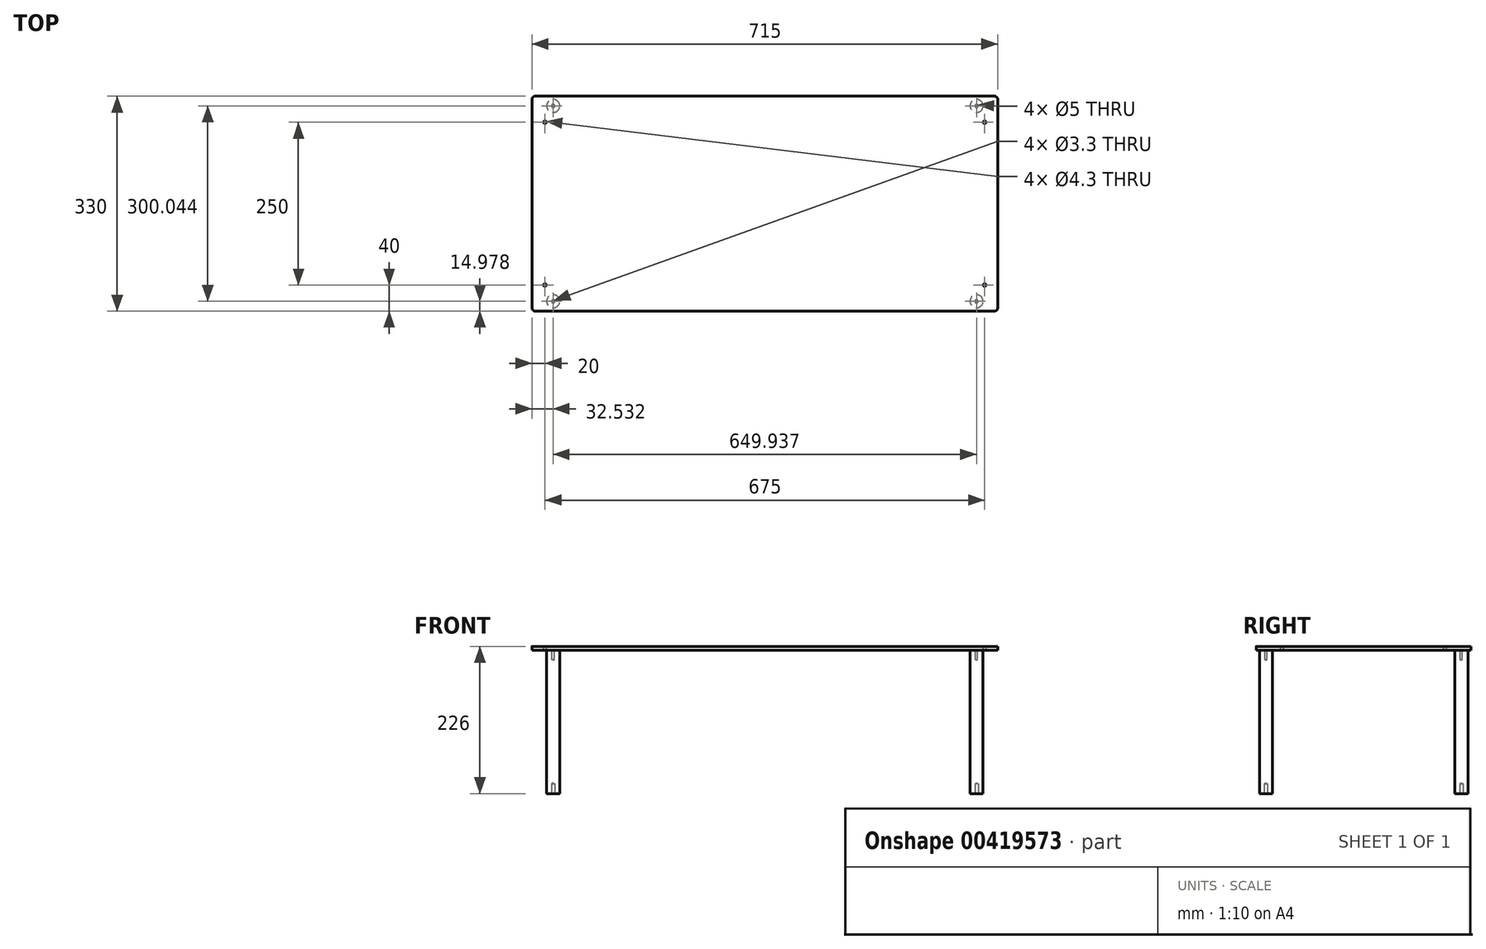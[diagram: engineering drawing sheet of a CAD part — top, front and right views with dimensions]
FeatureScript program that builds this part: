
annotation { "Feature Type Name" : "Feature", "Feature Type Description" : "" }
export const myFeature = defineFeature(function(context is Context, id is Id, definition is map)
    precondition{}
    {
        {
            var Q0;
            Q0=qCreatedBy(makeId("Top.planeOp"),FACE);
            var sketch = newSketch(context, id + "F0", { "sketchPlane" : qUnion([Q0])});
            skLineSegment(sketch, "E0.bottom", {"start": v(352.5, 165) * mm, "end": v(-352.5, 165) * mm});
            skLineSegment(sketch, "E0.top", {"start": v(352.5, -165) * mm, "end": v(-352.5, -165) * mm});
            skLineSegment(sketch, "E0.left", {"start": v(357.5, 160) * mm, "end": v(357.5, -160) * mm});
            skLineSegment(sketch, "E0.right", {"start": v(-357.5, 160) * mm, "end": v(-357.5, -160) * mm});
            skPoint(sketch, "E0.middle", {"position": v(0, 0) * mm});
            skPoint(sketch, "E1.visualSharp", {"position": v(-357.5, 165) * mm});
            skArc(sketch, "E1.filletArc", {"start": v(-352.5, 165) * mm, "mid": v(-356.04, 163.54) * mm, "end": v(-357.5, 160) * mm});
            skPoint(sketch, "E2.visualSharp", {"position": v(-357.5, -165) * mm});
            skArc(sketch, "E2.filletArc", {"start": v(-357.5, -160) * mm, "mid": v(-356.04, -163.54) * mm, "end": v(-352.5, -165) * mm});
            skPoint(sketch, "E3.visualSharp", {"position": v(357.5, 165) * mm});
            skArc(sketch, "E3.filletArc", {"start": v(357.5, 160) * mm, "mid": v(356.04, 163.54) * mm, "end": v(352.5, 165) * mm});
            skPoint(sketch, "E4.visualSharp", {"position": v(357.5, -165) * mm});
            skArc(sketch, "E4.filletArc", {"start": v(352.5, -165) * mm, "mid": v(356.04, -163.54) * mm, "end": v(357.5, -160) * mm});
            skPoint(sketch, "E5", {"position": v(-337.5, -125) * mm});
            skPoint(sketch, "E6.MirrorP", {"position": v(337.5, -125) * mm});
            skPoint(sketch, "E7.MirrorP", {"position": v(-337.5, 125) * mm});
            skPoint(sketch, "E8.MirrorP", {"position": v(337.5, 125) * mm});
            skCircle(sketch, "E9", {"center": v(-337.5, -125) * mm, "radius": 2.15 * mm});
            skCircle(sketch, "E10.MirrorC", {"center": v(337.5, -125) * mm, "radius": 2.15 * mm});
            skCircle(sketch, "E11.MirrorC", {"center": v(-337.5, 125) * mm, "radius": 2.15 * mm});
            skCircle(sketch, "E12.MirrorC", {"center": v(337.5, 125) * mm, "radius": 2.15 * mm});
            skSolve(sketch);
        }
        {
            var Q0;
            Q0=makeQuery(id+"F0.imprint","IMPRINT",FACE,{"disambiguationData":[TD([[makeQuery(id+"F0.imprint","IMPRINT",EDGE,{"derivedFrom":sQuery(id+"F0.wireOp",EDGE,"E0.bottom")}),1.0]])]});
            extrude(context, id + "F1", {"entities" : qUnion([Q0]), "oppositeDirection" : true, "depth" : 6 * mm});
        }
        {
            var Q0;
            Q0=makeQuery(id+"F1.opExtrude","CAP_FACE",FACE,{"disambiguationData":[OSD([sQuery(id+"F0.wireOp",EDGE,"E0.bottom"),sQuery(id+"F0.wireOp",EDGE,"E0.top"),sQuery(id+"F0.wireOp",EDGE,"E0.left"),sQuery(id+"F0.wireOp",EDGE,"E0.right"),sQuery(id+"F0.wireOp",EDGE,"E1.filletArc"),sQuery(id+"F0.wireOp",EDGE,"E2.filletArc"),sQuery(id+"F0.wireOp",EDGE,"E3.filletArc"),sQuery(id+"F0.wireOp",EDGE,"E4.filletArc")])],"isStart":false});
            var sketch = newSketch(context, id + "F2", { "sketchPlane" : qUnion([Q0])});
            skCircle(sketch, "E13", {"center": v(-324.97, 150.02) * mm, "radius": 10 * mm});
            skSolve(sketch);
        }
        {
            var Q0;
            Q0 = qSketchRegion(id + "F2", true);
            extrude(context, id + "F3", {"entities" : qUnion([Q0]), "depth" : 220 * mm});
        }
        {
            var Q0;
            Q0=makeQuery(id+"F3.opExtrude","CAP_FACE",FACE,{"disambiguationData":[OSD([sQuery(id+"F2.wireOp",EDGE,"E13")])],"isStart":false});
            var sketch = newSketch(context, id + "F4", { "sketchPlane" : qUnion([Q0])});
            skPoint(sketch, "E14", {"position": v(-324.97, 150.02) * mm});
            skSolve(sketch);
        }
        {
            var Q0;
            Q0=sQuery(id+"F4.wireOp",VERTEX,"E14");
            var Q1;
            Q1=makeQuery(id+"F3.opExtrude","SWEPT_BODY",BODY,{"disambiguationData":[OSD([sQuery(id+"F2.wireOp",EDGE,"E13")])]});
            hole(context, id + "F5", {"style" : HoleStyle.SIMPLE, "endStyle" : HoleEndStyle.BLIND, "standardTappedOrClearance" : lookupTablePath({ "standard" : "ISO", "engagement" : "75%", "pitch" : "1 mm", "size" : "M6", "type" : "Tapped" }), "standardBlindInLast" : lookupTablePath({ "standard" : "ISO", "engagement" : "75%", "pitch" : "1 mm", "size" : "M6", "type" : "Tapped" }), "holeDiameter" : 5 * mm, "showTappedDepth" : true, "holeDepth" : 15 * mm, "isTappedThrough" : true, "tappedDepth" : 12 * mm, "tapClearance" : 3, "startFromSketch" : true, "locations" : qUnion([Q0]), "scope" : qUnion([Q1]), "majorDiameter" : 6 * mm});
        }
        {
            var Q0;
            Q0=sQuery(id+"F2.wireOp",VERTEX,"E13.center");
            var Q1;
            Q1=makeQuery(id+"F3.opExtrude","SWEPT_BODY",BODY,{"disambiguationData":[OSD([sQuery(id+"F2.wireOp",EDGE,"E13")])]});
            hole(context, id + "F6", {"style" : HoleStyle.SIMPLE, "endStyle" : HoleEndStyle.BLIND, "oppositeDirection" : true, "standardTappedOrClearance" : lookupTablePath({ "standard" : "ISO", "engagement" : "75%", "pitch" : "0.7 mm", "size" : "M4", "type" : "Tapped" }), "standardBlindInLast" : lookupTablePath({ "standard" : "ISO", "engagement" : "75%", "pitch" : "0.7 mm", "size" : "M4", "type" : "Tapped" }), "holeDiameter" : 3.3 * mm, "showTappedDepth" : true, "holeDepth" : 14.1 * mm, "isTappedThrough" : true, "tappedDepth" : 12 * mm, "tapClearance" : 3, "startFromSketch" : true, "locations" : qUnion([Q0]), "scope" : qUnion([Q1]), "majorDiameter" : 4 * mm});
        }
        {
            var Q0;
            Q0=makeQuery(id+"F3.opExtrude","SWEPT_BODY",BODY,{"disambiguationData":[OSD([sQuery(id+"F2.wireOp",EDGE,"E13")])]});
            var Q1;
            Q1=qCreatedBy(makeId("Right.planeOp"),FACE);
            mirror(context, id + "F7", {"entities" : qUnion([Q0]), "mirrorPlane" : qUnion([Q1])});
        }
        {
            var Q0;
            Q0=makeQuery(id+"F3.opExtrude","SWEPT_BODY",BODY,{"disambiguationData":[OSD([sQuery(id+"F2.wireOp",EDGE,"E13")])]});
            var Q1;
            Q1=makeQuery(id+"F7.opPattern","COPY",BODY,{"derivedFrom":makeQuery(id+"F3.opExtrude","SWEPT_BODY",BODY,{"disambiguationData":[OSD([sQuery(id+"F2.wireOp",EDGE,"E13")])]}),"instanceName":"1"});
            var Q2;
            Q2=qCreatedBy(makeId("Front.planeOp"),FACE);
            mirror(context, id + "F8", {"entities" : qUnion([Q0, Q1]), "mirrorPlane" : qUnion([Q2])});
        }
    });
